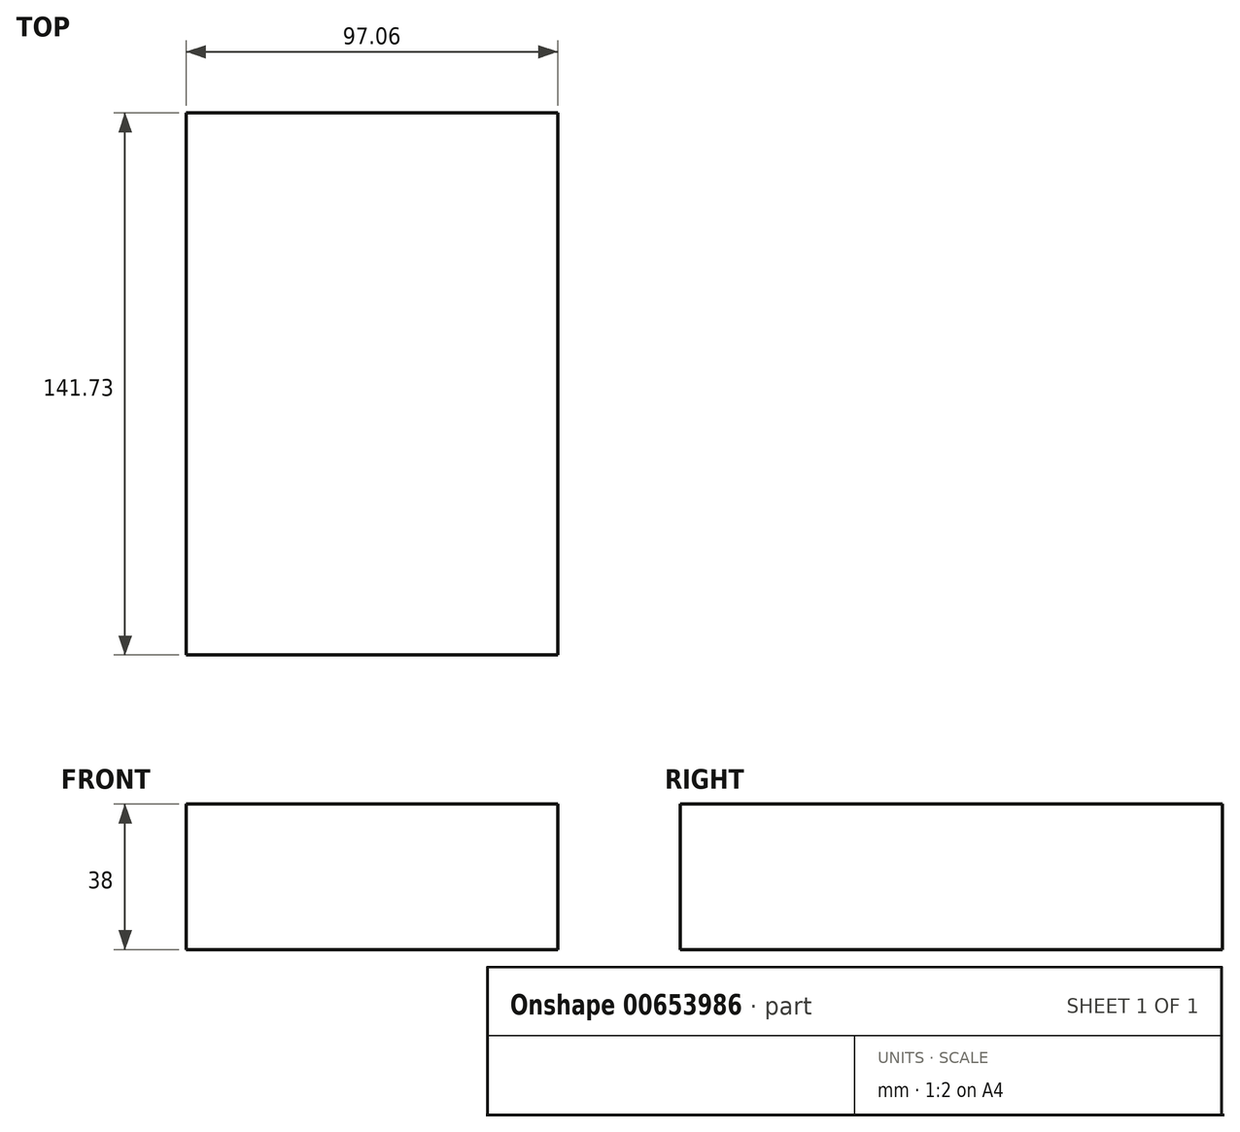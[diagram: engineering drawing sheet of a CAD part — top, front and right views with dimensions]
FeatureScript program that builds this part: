
annotation { "Feature Type Name" : "Feature", "Feature Type Description" : "" }
export const myFeature = defineFeature(function(context is Context, id is Id, definition is map)
    precondition{}
    {
        {
            var Q0;
            Q0=qCreatedBy(makeId("Top.planeOp"),FACE);
            var sketch = newSketch(context, id + "F0", { "sketchPlane" : qUnion([Q0])});
            skLineSegment(sketch, "E0.bottom", {"start": v(0, 0) * mm, "end": v(97.06, 0) * mm});
            skLineSegment(sketch, "E0.top", {"start": v(0, -141.73) * mm, "end": v(97.06, -141.73) * mm});
            skLineSegment(sketch, "E0.left", {"start": v(0, 0) * mm, "end": v(0, -141.73) * mm});
            skLineSegment(sketch, "E0.right", {"start": v(97.06, 0) * mm, "end": v(97.06, -141.73) * mm});
            skSolve(sketch);
        }
        {
            var Q0;
            Q0=makeQuery(id+"F0.imprint","IMPRINT",FACE,{"disambiguationData":[TD([[makeQuery(id+"F0.imprint","IMPRINT",EDGE,{"derivedFrom":sQuery(id+"F0.wireOp",EDGE,"E0.bottom")}),-1.0]])]});
            extrude(context, id + "F1", {"entities" : qUnion([Q0]), "depth" : 38 * mm, "offsetDistance" : 25.4 * mm});
        }
    });
